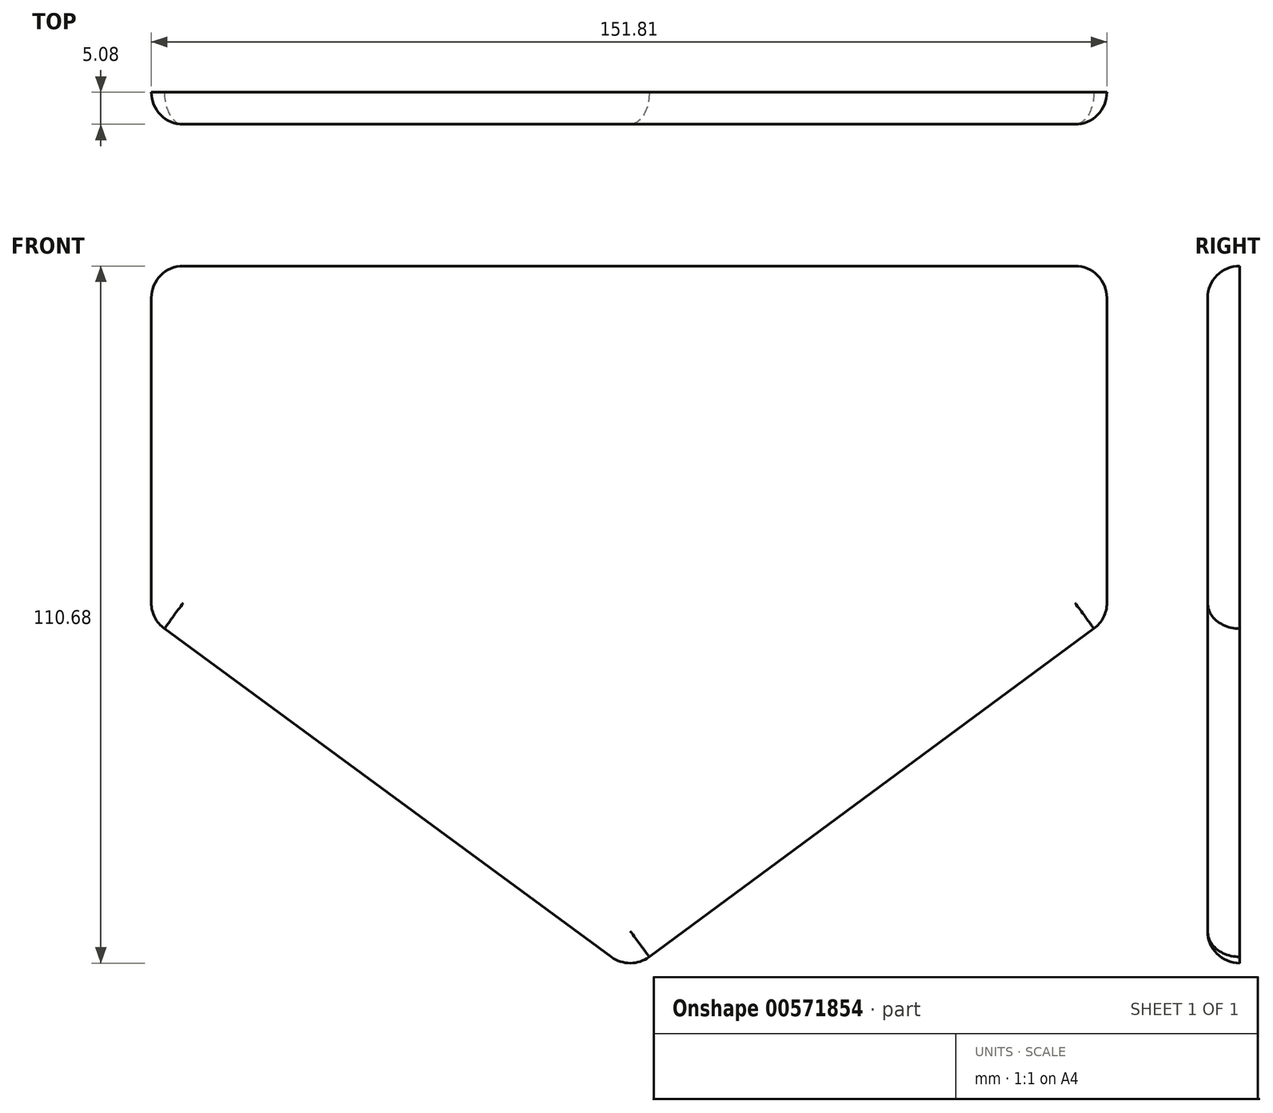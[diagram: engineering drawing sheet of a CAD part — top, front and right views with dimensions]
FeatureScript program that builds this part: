
annotation { "Feature Type Name" : "Feature", "Feature Type Description" : "" }
export const myFeature = defineFeature(function(context is Context, id is Id, definition is map)
    precondition{}
    {
        {
            var Q0;
            Q0=qCreatedBy(makeId("Front.planeOp"),FACE);
            var sketch = newSketch(context, id + "F0", { "sketchPlane" : qUnion([Q0])});
            skLineSegment(sketch, "E0", {"start": v(-76.1, 56.05) * mm, "end": v(75.71, 56.05) * mm});
            skLineSegment(sketch, "E1", {"start": v(75.71, 56.05) * mm, "end": v(75.71, 0) * mm});
            skLineSegment(sketch, "E2", {"start": v(75.71, 0) * mm, "end": v(0, -55.85) * mm});
            skLineSegment(sketch, "E3", {"start": v(0, -55.85) * mm, "end": v(-76.1, 0) * mm});
            skLineSegment(sketch, "E4", {"start": v(-76.1, 0) * mm, "end": v(-76.1, 56.05) * mm});
            skLineSegment(sketch, "E5", {"start": v(75.71, 0) * mm, "end": v(75.71, -55.85) * mm});
            skLineSegment(sketch, "E6", {"start": v(75.71, -55.85) * mm, "end": v(0, -55.85) * mm});
            skLineSegment(sketch, "E7", {"start": v(-76.1, -55.85) * mm, "end": v(-76.1, 0) * mm});
            skSolve(sketch);
        }
        {
            var Q0;
            Q0=makeQuery(id+"F0.imprint","IMPRINT",FACE,{"disambiguationData":[TD([[makeQuery(id+"F0.imprint","IMPRINT",EDGE,{"derivedFrom":sQuery(id+"F0.wireOp",EDGE,"E0")}),-1.0]])]});
            extrude(context, id + "F1", {"entities" : qUnion([Q0]), "depth" : 5.08 * mm, "offsetDistance" : 25.4 * mm});
        }
        {
            var Q0;
            Q0=makeQuery(id+"F1.opExtrude","CAP_EDGE",EDGE,{"disambiguationData":[OSD([sQuery(id+"F0.wireOp",EDGE,"E2")])],"isStart":false});
            fillet(context, id + "F2", {"entities" : qUnion([Q0]), "radius" : 5.08 * mm, "tangentPropagation" : true, "allowEdgeOverflow" : false});
        }
        {
            var Q0;
            Q0=makeQuery(id+"F1.opExtrude","CAP_EDGE",EDGE,{"disambiguationData":[OSD([sQuery(id+"F0.wireOp",EDGE,"E3")])],"isStart":false});
            fillet(context, id + "F3", {"entities" : qUnion([Q0]), "radius" : 5.08 * mm, "tangentPropagation" : true, "allowEdgeOverflow" : false});
        }
        {
            var Q0;
            Q0=makeQuery(id+"F1.opExtrude","CAP_EDGE",EDGE,{"disambiguationData":[OSD([sQuery(id+"F0.wireOp",EDGE,"E1")])],"isStart":false});
            fillet(context, id + "F4", {"entities" : qUnion([Q0]), "radius" : 5.08 * mm, "tangentPropagation" : true, "allowEdgeOverflow" : false});
        }
        {
            var Q0;
            Q0=makeQuery(id+"F1.opExtrude","CAP_EDGE",EDGE,{"disambiguationData":[OSD([sQuery(id+"F0.wireOp",EDGE,"E4")])],"isStart":false});
            fillet(context, id + "F5", {"entities" : qUnion([Q0]), "radius" : 5.08 * mm, "tangentPropagation" : true, "allowEdgeOverflow" : false});
        }
        {
            var Q0;
            Q0=makeQuery(id+"F1.opExtrude","CAP_EDGE",EDGE,{"disambiguationData":[OSD([sQuery(id+"F0.wireOp",EDGE,"E0")])],"isStart":false});
            fillet(context, id + "F6", {"entities" : qUnion([Q0]), "radius" : 5.08 * mm, "tangentPropagation" : true, "allowEdgeOverflow" : false});
        }
    });
